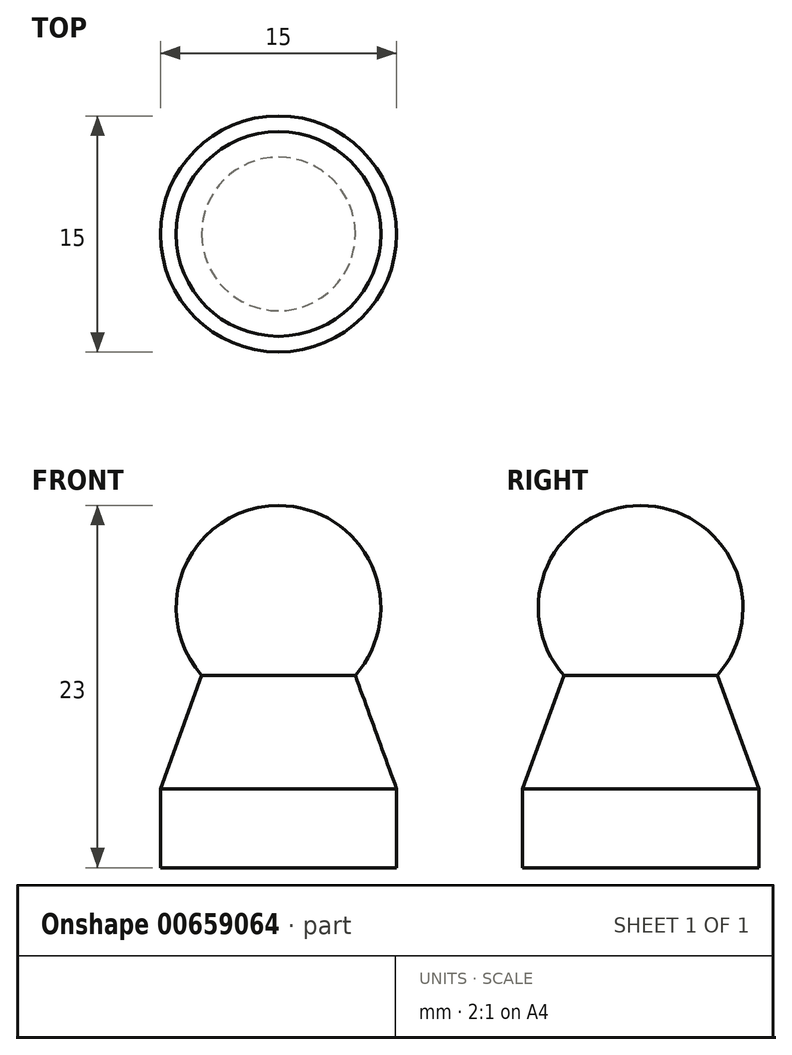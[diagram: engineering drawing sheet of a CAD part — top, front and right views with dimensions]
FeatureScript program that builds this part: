
annotation { "Feature Type Name" : "Feature", "Feature Type Description" : "" }
export const myFeature = defineFeature(function(context is Context, id is Id, definition is map)
    precondition{}
    {
        {
            var Q0;
            Q0=qCreatedBy(makeId("Top.planeOp"),FACE);
            var sketch = newSketch(context, id + "F0", { "sketchPlane" : qUnion([Q0])});
            skCircle(sketch, "E0", {"center": v(0, 0) * mm, "radius": 7.5 * mm});
            skSolve(sketch);
        }
        {
            var Q0;
            Q0=qSketchRegion(id+"F0",true);
            extrude(context, id + "F1", {"entities" : qUnion([Q0]), "depth" : 5 * mm, "offsetDistance" : 25 * mm});
        }
        {
            var Q0;
            Q0=makeQuery(id+"F1.opExtrude","CAP_FACE",FACE,{"disambiguationData":[OSD([sQuery(id+"F0.wireOp",EDGE,"E0")])],"isStart":false});
            extrude(context, id + "F2", {"entities" : qUnion([Q0]), "operationType" : NewBodyOperationType.ADD, "depth" : 10 * mm, "offsetDistance" : 25 * mm, "hasDraft" : true, "draftAngle" : 20 * degree, "draftPullDirection" : true});
        }
        {
            var Q0;
            Q0=qCreatedBy(makeId("Front.planeOp"),FACE);
            var sketch = newSketch(context, id + "F3", { "sketchPlane" : qUnion([Q0])});
            skArc(sketch, "E1", {"start": v(0, 10) * mm, "mid": v(6.5, 16.5) * mm, "end": v(0, 23) * mm});
            skLineSegment(sketch, "E2.0", {"start": v(-7.5, 5) * mm, "end": v(7.5, 5) * mm, "construction": true});
            skLineSegment(sketch, "E3", {"start": v(0, 10) * mm, "end": v(0, 23) * mm});
            skSolve(sketch);
        }
        {
            var Q0;
            Q0=qSketchRegion(id+"F3",true);
            var Q1;
            Q1=sQuery(id+"F3.wireOp",EDGE,"E3");
            revolve(context, id + "F4", {"operationType" : NewBodyOperationType.ADD, "entities" : qUnion([Q0]), "axis" : qUnion([Q1]), "revolveType" : RevolveType.FULL});
        }
    });
